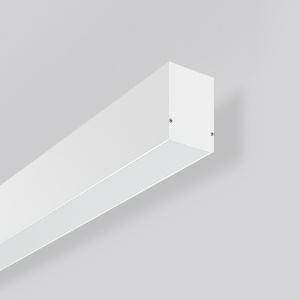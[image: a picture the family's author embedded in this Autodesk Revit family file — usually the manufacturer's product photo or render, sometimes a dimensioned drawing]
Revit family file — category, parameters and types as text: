
# Revit family: less_is_more_50_312614_002_1_76_94f7
name_source: partatom
category: Lighting Fixtures
units: mm (PartAtom-declared; Revit-internal decimal feet)

## family parameters
Cut with Voids When Loaded = No
Host = Face
Light Source = No
Part Type = Normal
Room Calculation Point = No
Round Connector Dimension = Use Diameter
Shared = No

## types (1)
- LESS IS MORE 50 (1 x LED Modul 840, 4800 lm, 4000)
    Apparent Load = 34 VA
    CIE Flux Codes = 48 80 96 50 100
    Color Rendering = 80
    Color Temperature = 4000
    Default Elevation = 1800 mm
    Description = Series: LESS IS MORE 50
Linear wall luminaires. Housing: extruded aluminium profile, powder-coated. End cap aluminium powder-coated. Diffuser made of non-yellowing plastic (PMMA), opal. Direct 50%, indirect 50% light emission. Suitable for Wall (surface). LED unit with integrated converter interchangeable and removable. Suitable for through-wiring. With sensors or as a safety luminaire on request. 
Colour: traffic white, matt (RAL 9016)
Length: 1967 mm
Width: 67 mm
Height: 75 mm
Lamp: LED
Socket: without socket
Colour temperature: 4000K
Colour rendering index (CRI): 80
Light source: LED
Socket lamp2: Without base
Colour temperature: 4000K
Colour rendering index (CRI) 2: 80
System power: 34 W
Rated luminous flux: 4800 lm
Luminous efficiency: 141 lm/W
Control gear: Converter, dimmable, DALI
Control gear: Converter, dimmable, DALI
Protection class: I
Type of protection: IP 20
    Height = 75 mm
    Lamp = 1 x LED Modul 840
    Lamp Light Flux = 4800 lm
    Lamp count = 1
    Length = 1967 mm
    Lifetime = 50000 h
    Luminous efficacy = 141 lm/W
    Manufacturer = RZB
    ModVariant = No
    Model = 312614.002.1.76
    Mounting Place = Wall
    Mounting Type = Surface mounted
    Number of Poles = 1
    OnlyDefault = Yes
    Power Factor = 1
    Product Name = LESS IS MORE 50
    Product group = Surface mounted LED linear luminaires
    ProductGroupID = 2007
    Protection Class = Protection class I
    Protection Degree = IP 20
    RLX_Detail_Level = 1
    RLX_Emergency_Light_Flux = 0 lm
    RLX_Emergency_Type = 0
    RLX_Emergency_Type_DB = No
    RlxData = <blob elided: 39617 chars, md5=81de2ab2>
    Socket = socket
    Standby Power = 0 W
    System Light Flux = 4800 lm
    System Power = 34 W
    Type Comments = Product without accessories
    Type Image = 312606.002.jpg
    URL = http://relux.com
    VarID = ---
    Voltage = 0 V
    Weight = 0.00 kg
    Width = 67 mm

## geometry (parser evidence)
native form markers: Blend x4, Sweep x14
no freeform markers — native parametric forms only
